# Revit family: UM372LPL Banco Kube Luz Plus
name_source: partatom
category: Mobiliario
units: mm (PartAtom-declared; Revit-internal decimal feet)

## family parameters
Compartido = No
Corte con vacíos al cargar = No
Número OmniClass = 23.40.20.00
Punto de cálculo de habitación = No
Se basa en plano de trabajo = No
Siempre vertical = Sí
Título OmniClass = General Furniture and Specialties

## types (1)
- UM372LL Banco Kube Luz Plus
    Acabado Listones = Lignus, protector fungicida, insecticida e hidrófugo.
    Acabado bancada = Color gris granítico de aspecto rugoso.
    Accessibilidad = Sí
    Altura asiento = 493 mm  [stored 1.61745 ft]
    Altura total = 775 mm  [stored 2.54265 ft]
    Ancho = 500 mm  [stored 1.64042 ft]
    Baliza empotrada = Baliza empotrada en el banco, material cuerpo: aluminio, material del difusor: cristal matizado, acabado en acero
inoxidable. Lámpara LED con potencia de 4,5W, alimentación de 220V-240V AC, equipo electrónico, Clase 1, IP:65,
IK:09, temperatura de color: 3000k.
    Comentarios de tipo = Hormigón prefabricado color gris granítico de aspecto rugoso.Se puede colocar en elementos aislados o en grupos.Hormigón prefabricado color gris granítico de aspecto rugoso.Se puede colocar en elementos aislados o en grupos. Hormigón prefabricado color gris granítico de aspecto rugoso.Se puede colocar en elementos aislados o en grupos.Baliza empotrada en el banco, material cuerpo: aluminio, material del difusor: cristal matizado, acabado en acero
inoxidable. Lámpara LED con potencia de 4,5W, alimentación de 220V-240V AC, equipo electrónico, Clase 1, IP:65,
IK:09, temperatura de color: 3000k.
    Fabricante = BENITO
    Ficha tecnica = http://www.benito.com
    Instalación = Apoyado por su propio peso.
    Largo = 2000 mm  [stored 6.56168 ft]
    Material bancada = Hormigón prefabricado.
    Material listones = Madera Tropical
    Modelo = Banco Kube Luz Plus
    Referencia = UM372LPL
    URL = http://www.benito.com
    URL Producto = http://www.benito.com

note: [stored X ft] marks values corroborated as IEEE doubles in the binary element streams (Revit-internal decimal feet)

## geometry (parser evidence)
native form markers: Blend x4
no freeform markers — native parametric forms only
